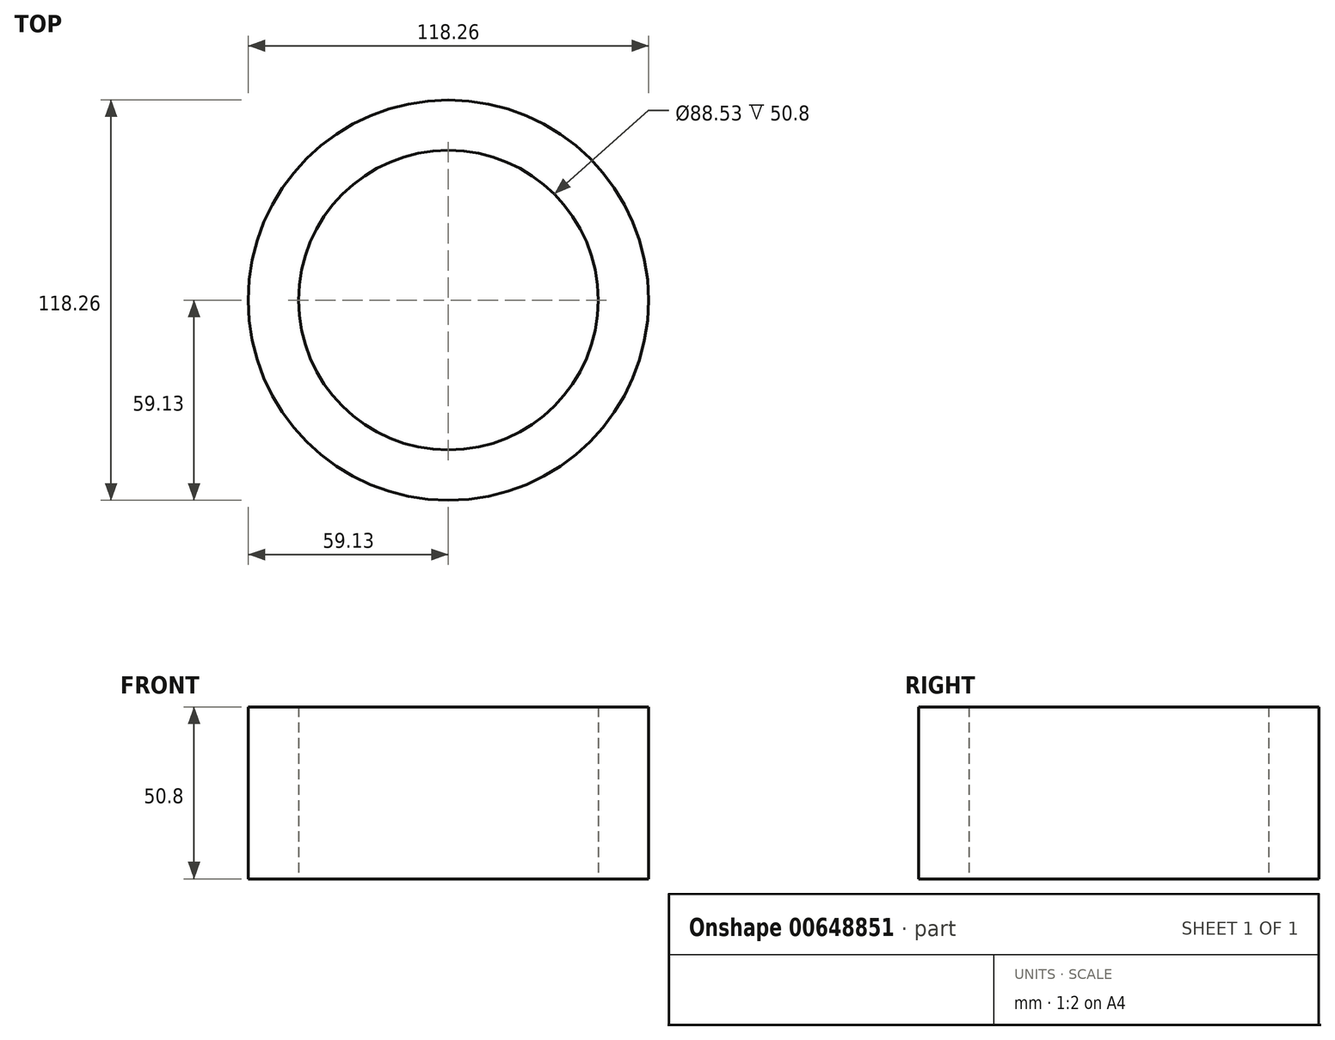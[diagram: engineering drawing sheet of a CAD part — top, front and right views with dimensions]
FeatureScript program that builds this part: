
annotation { "Feature Type Name" : "Feature", "Feature Type Description" : "" }
export const myFeature = defineFeature(function(context is Context, id is Id, definition is map)
    precondition{}
    {
        {
            var Q0;
            Q0=qCreatedBy(makeId("Top.planeOp"),FACE);
            var sketch = newSketch(context, id + "F0", { "sketchPlane" : qUnion([Q0])});
            skCircle(sketch, "E0", {"center": v(0, 0) * mm, "radius": 59.13 * mm});
            skCircle(sketch, "E1", {"center": v(0, 0) * mm, "radius": 44.26 * mm});
            skSolve(sketch);
        }
        {
            var Q0;
            Q0 = qSketchRegion(id + "Fd5CCDdSc1ckE5x_0", true);
            var Q1;
            Q1=makeQuery(id+"F0.imprint","IMPRINT",FACE,{"disambiguationData":[TD([[makeQuery(id+"F0.imprint","IMPRINT",EDGE,{"derivedFrom":sQuery(id+"F0.wireOp",EDGE,"E0")}),1.0]])]});
            extrude(context, id + "F1", {"entities" : qUnion([Q0, Q1]), "depth" : 50.8 * mm, "offsetDistance" : 25.4 * mm});
        }
    });
